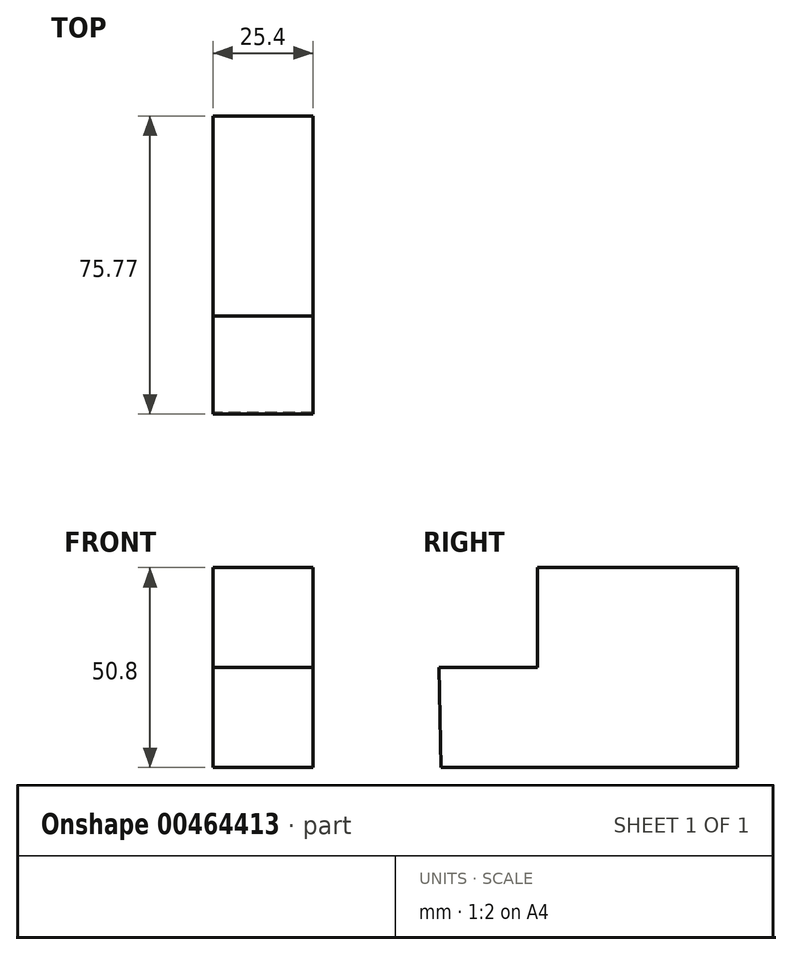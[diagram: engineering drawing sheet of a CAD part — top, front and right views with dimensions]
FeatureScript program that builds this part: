
annotation { "Feature Type Name" : "Feature", "Feature Type Description" : "" }
export const myFeature = defineFeature(function(context is Context, id is Id, definition is map)
    precondition{}
    {
        {
            var Q0;
            Q0=qCreatedBy(makeId("Right.planeOp"),FACE);
            var sketch = newSketch(context, id + "F0", { "sketchPlane" : qUnion([Q0])});
            skLineSegment(sketch, "E0", {"start": v(80.68, 63.68) * mm, "end": v(29.88, 63.68) * mm});
            skLineSegment(sketch, "E1", {"start": v(29.88, 63.68) * mm, "end": v(29.88, 38.27) * mm});
            skLineSegment(sketch, "E2", {"start": v(29.88, 38.27) * mm, "end": v(4.91, 38.27) * mm});
            skLineSegment(sketch, "E3", {"start": v(4.91, 38.27) * mm, "end": v(5.37, 12.88) * mm});
            skLineSegment(sketch, "E4", {"start": v(5.37, 12.88) * mm, "end": v(80.68, 12.88) * mm});
            skLineSegment(sketch, "E5", {"start": v(80.68, 12.88) * mm, "end": v(80.68, 63.68) * mm});
            skSolve(sketch);
        }
        {
            var Q0;
            Q0 = qSketchRegion(id + "F0", true);
            extrude(context, id + "F1", {"entities" : qUnion([Q0]), "depth" : 25.4 * mm});
        }
    });
